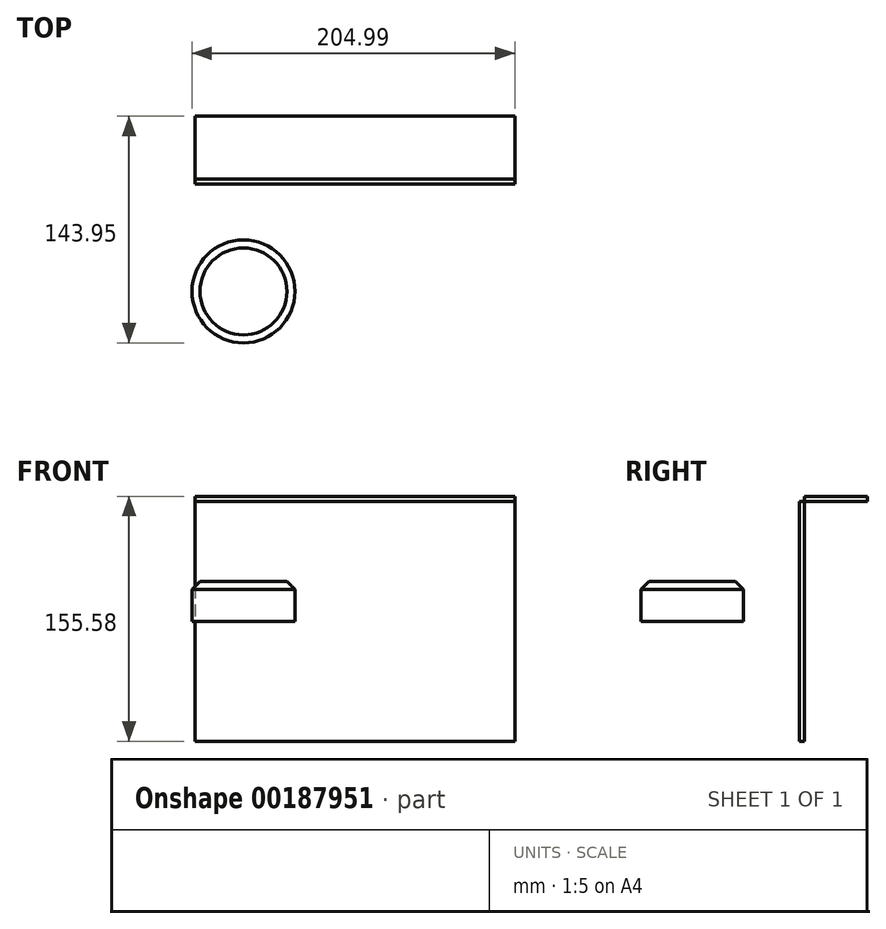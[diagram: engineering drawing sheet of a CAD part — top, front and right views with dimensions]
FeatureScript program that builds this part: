
annotation { "Feature Type Name" : "Feature", "Feature Type Description" : "" }
export const myFeature = defineFeature(function(context is Context, id is Id, definition is map)
    precondition{}
    {
        {
            var Q0;
            Q0=qCreatedBy(makeId("Front.planeOp"),FACE);
            var sketch = newSketch(context, id + "F0", { "sketchPlane" : qUnion([Q0])});
            skLineSegment(sketch, "E0.bottom", {"start": v(101.6, 76.2) * mm, "end": v(-101.6, 76.2) * mm});
            skLineSegment(sketch, "E0.top", {"start": v(101.6, -76.2) * mm, "end": v(-101.6, -76.2) * mm});
            skLineSegment(sketch, "E0.left", {"start": v(101.6, 76.2) * mm, "end": v(101.6, -76.2) * mm});
            skLineSegment(sketch, "E0.right", {"start": v(-101.6, 76.2) * mm, "end": v(-101.6, -76.2) * mm});
            skPoint(sketch, "E0.middle", {"position": v(0, 0) * mm});
            skSolve(sketch);
        }
        {
            var Q0;
            Q0 = qSketchRegion(id + "F0", true);
            extrude(context, id + "F1", {"entities" : qUnion([Q0]), "depth" : 3.17 * mm});
        }
        {
            var Q0;
            Q0=makeQuery(id+"F1.opExtrude","SWEPT_FACE",FACE,{"disambiguationData":[OSD([sQuery(id+"F0.wireOp",EDGE,"E0.bottom")])]});
            var sketch = newSketch(context, id + "F2", { "sketchPlane" : qUnion([Q0])});
            skLineSegment(sketch, "E1.bottom", {"start": v(-101.6, 0) * mm, "end": v(101.6, 0) * mm});
            skLineSegment(sketch, "E1.top", {"start": v(-101.6, 40.07) * mm, "end": v(101.6, 40.07) * mm});
            skLineSegment(sketch, "E1.left", {"start": v(-101.6, 0) * mm, "end": v(-101.6, 40.07) * mm});
            skLineSegment(sketch, "E1.right", {"start": v(101.6, 0) * mm, "end": v(101.6, 40.07) * mm});
            skSolve(sketch);
        }
        {
            var Q0;
            Q0=makeQuery(id+"F2.imprint","IMPRINT",FACE,{"disambiguationData":[TD([[makeQuery(id+"F2.imprint","IMPRINT",EDGE,{"derivedFrom":sQuery(id+"F2.wireOp",EDGE,"E1.bottom")}),-1.0]])]});
            extrude(context, id + "F3", {"entities" : qUnion([Q0]), "depth" : 3.17 * mm});
        }
        {
            var Q0;
            Q0=makeQuery(id+"F3.opExtrude","CAP_FACE",FACE,{"disambiguationData":[OSD([sQuery(id+"F2.wireOp",EDGE,"E1.bottom"),sQuery(id+"F2.wireOp",EDGE,"E1.top"),sQuery(id+"F2.wireOp",EDGE,"E1.left"),sQuery(id+"F2.wireOp",EDGE,"E1.right")])],"isStart":false});
            var sketch = newSketch(context, id + "F4", { "sketchPlane" : qUnion([Q0])});
            skCircle(sketch, "E2", {"center": v(-25.78, 23.62) * mm, "radius": 2.04 * mm});
            skSolve(sketch);
        }
        {
            var Q0;
            Q0=sQuery(id+"F4.wireOp",EDGE,"E2");
            extrude(context, id + "F7", {"bodyType" : ToolBodyType.SURFACE, "surfaceEntities" : qUnion([Q0]), "depth" : 25.4 * mm});
        }
        {
            var Q0;
            Q0=qCreatedBy(makeId("Top.planeOp"),FACE);
            var sketch = newSketch(context, id + "F5", { "sketchPlane" : qUnion([Q0])});
            skCircle(sketch, "E3", {"center": v(-70.72, -71.2) * mm, "radius": 32.67 * mm});
            skSolve(sketch);
        }
        {
            var Q0;
            Q0=makeQuery(id+"F5.imprint","IMPRINT",FACE,{"disambiguationData":[TD([[makeQuery(id+"F5.imprint","IMPRINT",EDGE,{"derivedFrom":sQuery(id+"F5.wireOp",EDGE,"E3")}),1.0]])]});
            extrude(context, id + "F6", {"entities" : qUnion([Q0]), "depth" : 25.4 * mm});
        }
        {
            var Q0;
            Q0=makeQuery(id+"F6.opExtrude","CAP_EDGE",EDGE,{"disambiguationData":[OSD([sQuery(id+"F5.wireOp",EDGE,"E3")])],"isStart":false});
            chamfer(context, id + "F8", {"entities" : qUnion([Q0]), "width" : 5.08 * mm, "tangentPropagation" : true});
        }
    });
